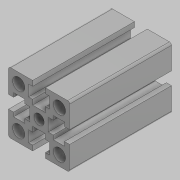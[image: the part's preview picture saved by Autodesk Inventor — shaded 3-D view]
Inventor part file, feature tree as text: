
AUTODESK INVENTOR PART (.ipt)
format: ipt  version: 2021.2 (Build 252289000, 289)  size: 211,456 bytes
history: native  units: in
note: dims shown in document units (in); Inventor stores cm internally (conversion verified against a paired STEP export)
features: other x2, extrude x1, sketch x1, projected_geometry x1
ambient origin geometry x8: Origin, YZ Plane, XZ Plane, XY Plane, X Axis, Y Axis, Z Axis, Center Point
bodies: Body1 (feature_tree)
feature tree (5):
  other  "ソリッド2"
  extrude  "押し出し1"  Depth=1.9685in
  sketch  "スケッチ2"
  projected_geometry  "投影ループ1"
  other  "ソリッド1"
